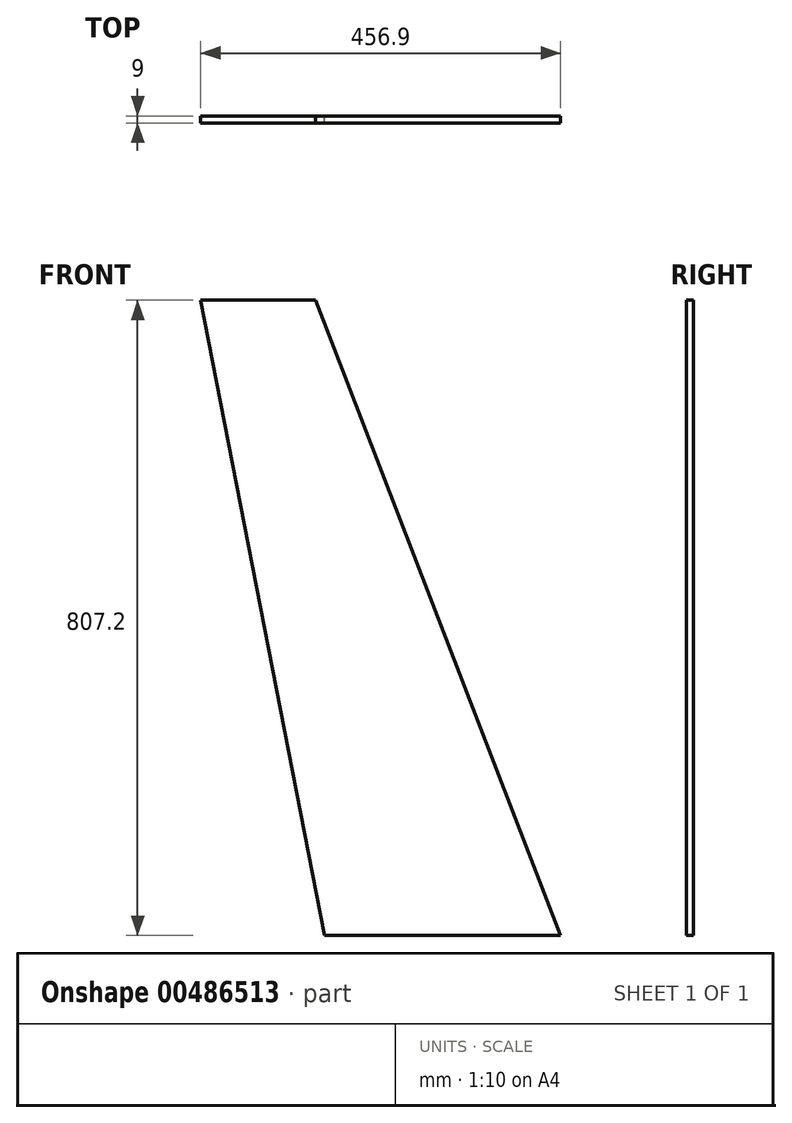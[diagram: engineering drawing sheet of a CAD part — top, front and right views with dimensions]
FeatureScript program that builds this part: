
annotation { "Feature Type Name" : "Feature", "Feature Type Description" : "" }
export const myFeature = defineFeature(function(context is Context, id is Id, definition is map)
    precondition{}
    {
        {
            var Q0;
            Q0=qCreatedBy(makeId("Front.planeOp"),FACE);
            var sketch = newSketch(context, id + "F0", { "sketchPlane" : qUnion([Q0])});
            skLineSegment(sketch, "E0", {"start": v(-156.9, 807.2) * mm, "end": v(-10.9, 807.2) * mm});
            skLineSegment(sketch, "E1", {"start": v(-10.9, 807.2) * mm, "end": v(300, 0) * mm});
            skLineSegment(sketch, "E2", {"start": v(300, 0) * mm, "end": v(0, 0) * mm});
            skLineSegment(sketch, "E3", {"start": v(0, 0) * mm, "end": v(-156.9, 807.2) * mm});
            skSolve(sketch);
        }
        {
            var Q0;
            Q0=makeQuery(id+"F0.imprint","IMPRINT",FACE,{"disambiguationData":[TD([[makeQuery(id+"F0.imprint","IMPRINT",EDGE,{"derivedFrom":sQuery(id+"F0.wireOp",EDGE,"E0")}),-1.0]])]});
            extrude(context, id + "F1", {"entities" : qUnion([Q0]), "depth" : 9 * mm, "offsetDistance" : 25 * mm});
        }
    });
